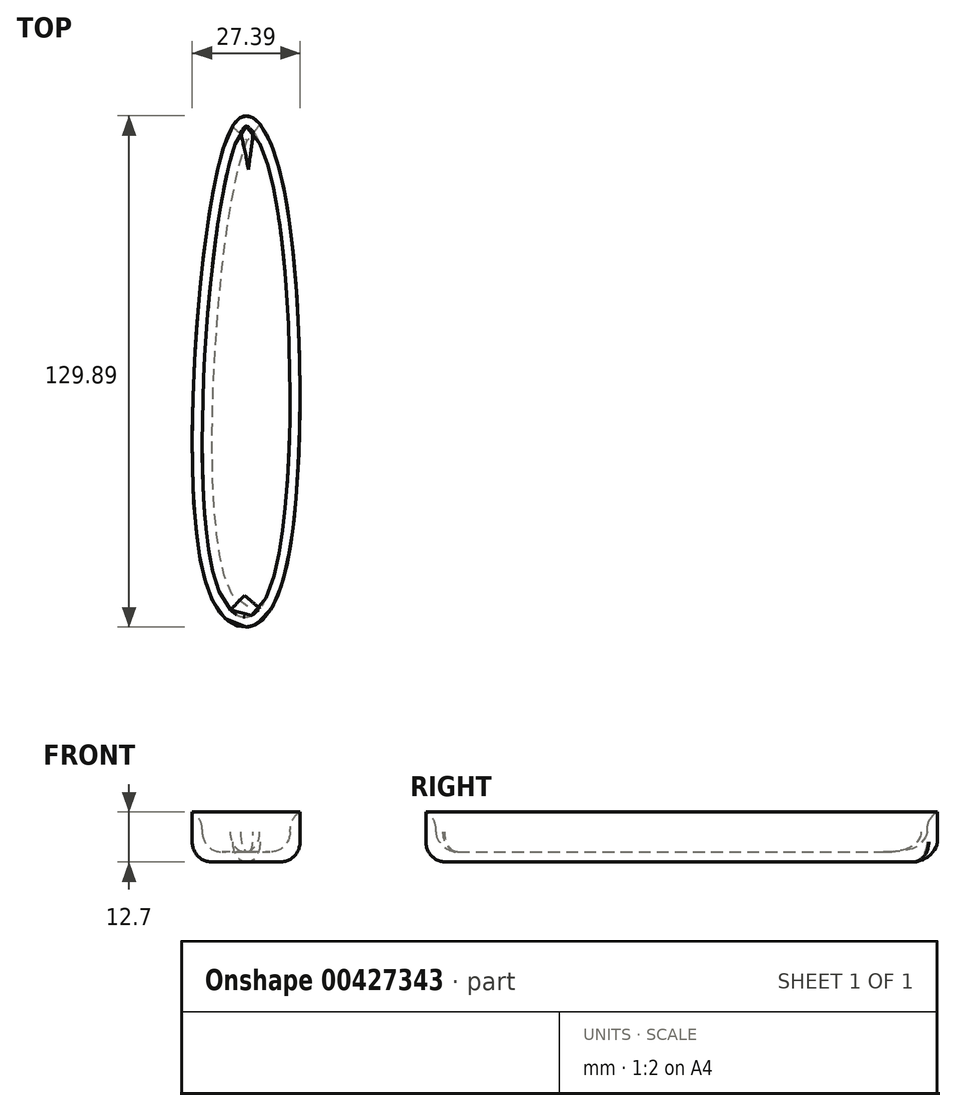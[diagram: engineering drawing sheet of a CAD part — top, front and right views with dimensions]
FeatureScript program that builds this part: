
annotation { "Feature Type Name" : "Feature", "Feature Type Description" : "" }
export const myFeature = defineFeature(function(context is Context, id is Id, definition is map)
    precondition{}
    {
        {
            var Q0;
            Q0=qCreatedBy(makeId("Top.planeOp"),FACE);
            var sketch = newSketch(context, id + "F0", { "sketchPlane" : qUnion([Q0])});
            skFitSpline(sketch, "E0", {"points": [v(0, -61.86) * mm, v(9.58, -49.49) * mm, v(8.6, 54.09) * mm, v(0, 68.02) * mm, v(-7.33, 53.96) * mm, v(-10.26, -50.56) * mm, v(0, -61.86) * mm]});
            skSolve(sketch);
        }
        {
            var Q0;
            Q0 = qSketchRegion(id + "F0", true);
            var Q1;
            Q1 = qSketchRegion(id + "Fe8tlgFzCPNEFho_1", true);
            extrude(context, id + "F1", {"entities" : qUnion([Q0, Q1]), "depth" : 12.7 * mm});
        }
        {
            var Q0;
            Q0=makeQuery(id+"F1.opExtrude","CAP_FACE",FACE,{"disambiguationData":[OSD([sQuery(id+"F0.wireOp",EDGE,"E0")])],"isStart":false});
            shell(context, id + "F2", {"entities" : qUnion([Q0]), "thickness" : 2.54 * mm});
        }
        {
            var Q0;
            {var subQ0=sQuery(id+"F0.wireOp",EDGE,"E0");Q0=makeQuery(id+"F2.opShell","OFFSET_EDGE",EDGE,{"disambiguationData":[OSD([subQ0]),TDD([makeQuery(id+"F1.opExtrude","CAP_EDGE",EDGE,{"disambiguationData":[OSD([subQ0])],"isStart":false})])]});}
            var Q1;
            {var subQ0=sQuery(id+"F0.wireOp",EDGE,"E0");Q1=makeQuery(id+"F2.opShell","OFFSET_EDGE",EDGE,{"disambiguationData":[OSD([subQ0]),TDD([makeQuery(id+"F1.opExtrude","CAP_EDGE",EDGE,{"disambiguationData":[OSD([subQ0])],"isStart":true})])]});}
            fillet(context, id + "F3", {"entities" : qUnion([Q0, Q1]), "radius" : 5.08 * mm, "tangentPropagation" : true, "allowEdgeOverflow" : false});
        }
        {
            var Q0;
            Q0=makeQuery(id+"F1.opExtrude","CAP_EDGE",EDGE,{"disambiguationData":[OSD([sQuery(id+"F0.wireOp",EDGE,"E0")])],"isStart":true});
            fillet(context, id + "F4", {"entities" : qUnion([Q0]), "radius" : 5.08 * mm, "tangentPropagation" : true, "allowEdgeOverflow" : false});
        }
    });
